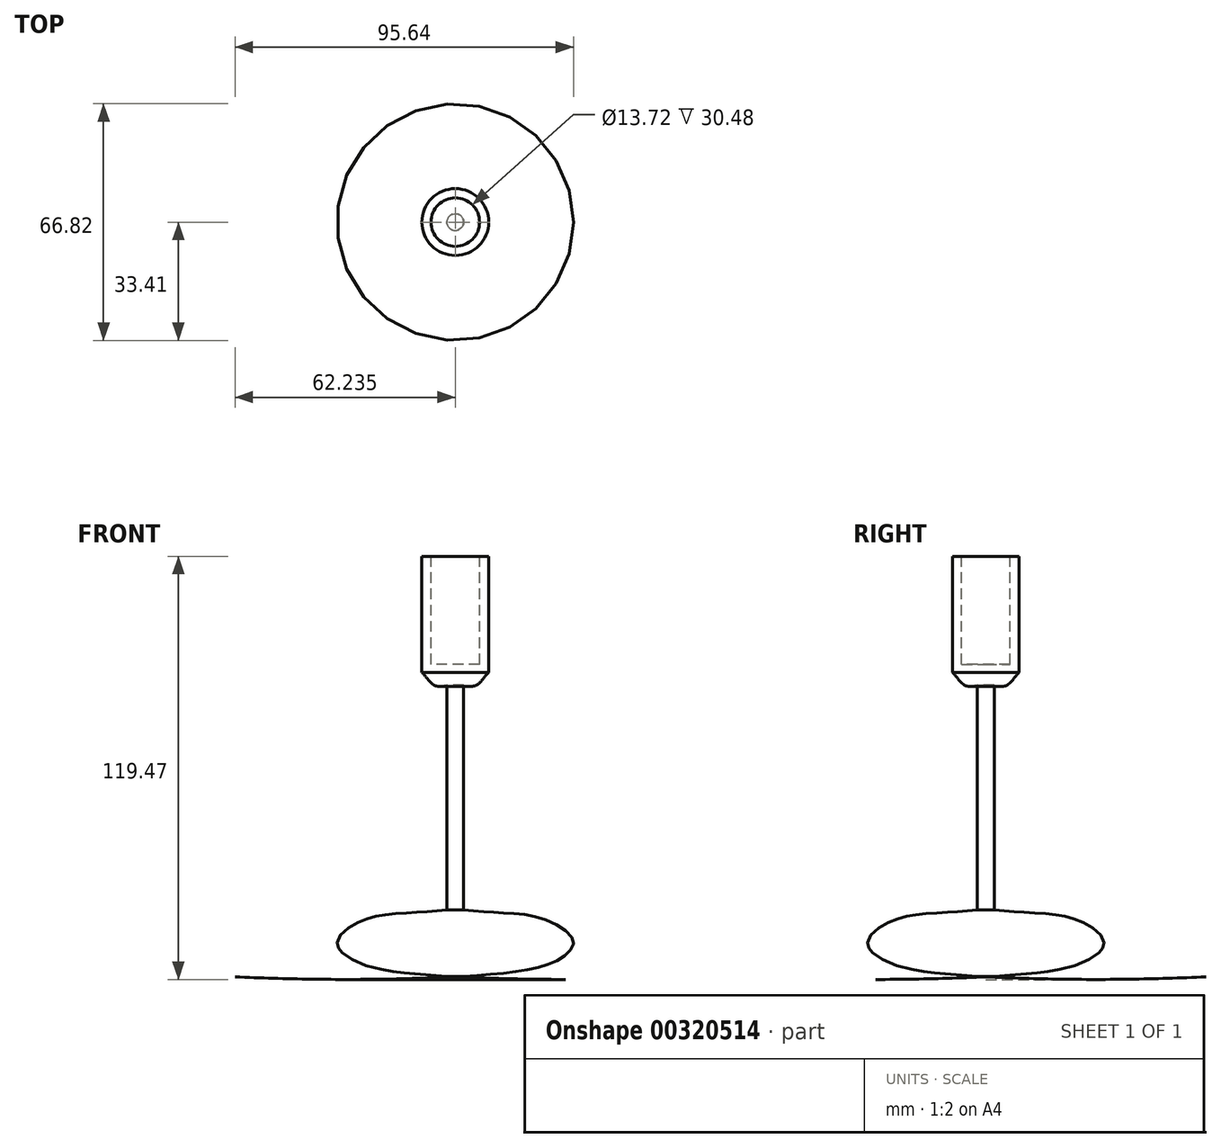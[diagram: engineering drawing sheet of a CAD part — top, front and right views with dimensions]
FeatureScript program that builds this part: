
annotation { "Feature Type Name" : "Feature", "Feature Type Description" : "" }
export const myFeature = defineFeature(function(context is Context, id is Id, definition is map)
    precondition{}
    {
        {
            var Q0;
            Q0=qCreatedBy(makeId("Front.planeOp"),FACE);
            var sketch = newSketch(context, id + "F0", { "sketchPlane" : qUnion([Q0])});
            skFitSpline(sketch, "E0", {"points": [v(7.08, -74.44) * mm, v(-10.6, -72.64) * mm, v(-20.84, -69.06) * mm, v(-23.91, -64.45) * mm, v(-15.72, -58.3) * mm, v(-3.68, -56.5) * mm, v(7.08, -55.74) * mm], "startDerivative": vector(-87.87, 5.95) * mm, "endDerivative": vector(64.33, 5.15) * mm});
            skPoint(sketch, "E1.1.internal.orphan", {"position": v(21.42, -74.44) * mm});
            skFitSpline(sketch, "E2", {"points": [v(11.95, -55.48) * mm, v(22.7, -56) * mm, v(35, -58.56) * mm, v(42.17, -62.65) * mm, v(41.14, -68.8) * mm, v(32.18, -72.13) * mm, v(21.42, -74.44) * mm, v(7.08, -74.44) * mm], "startDerivative": vector(71.75, -0.74) * mm, "endDerivative": vector(-88.62, 4.6) * mm});
            skLineSegment(sketch, "E3", {"start": v(7.08, -55.74) * mm, "end": v(7.08, 7.76) * mm});
            skFitSpline(sketch, "E4", {"points": [v(7.08, 7.76) * mm, v(3.5, 7.76) * mm, v(0, 11.39) * mm], "startDerivative": vector(-7.64, -1.07) * mm, "endDerivative": vector(-6.54, 5.6) * mm});
            skLineSegment(sketch, "E5", {"start": v(0, 11.39) * mm, "end": v(0, 44.15) * mm});
            skFitSpline(sketch, "E6", {"points": [v(11.95, 8.02) * mm, v(16.04, 8.02) * mm, v(19.63, 11.39) * mm], "startDerivative": vector(8.48, -1.02) * mm, "endDerivative": vector(6.9, 5.11) * mm});
            skPoint(sketch, "E7.4.internal.orphan", {"position": v(19.63, 44.15) * mm});
            skFitSpline(sketch, "E8", {"points": [v(0, 44.15) * mm, v(8.1, 44.15) * mm, v(19.63, 44.15) * mm], "startDerivative": vector(16.99, 0) * mm, "endDerivative": vector(22.12, 0) * mm});
            skLineSegment(sketch, "E9", {"start": v(2.58, 44.15) * mm, "end": v(2.58, 13.67) * mm});
            skLineSegment(sketch, "E10", {"start": v(9.44, 13.67) * mm, "end": v(2.58, 13.67) * mm});
            skLineSegment(sketch, "E11", {"start": v(9.44, 53.37) * mm, "end": v(9.44, -81) * mm, "construction": true});
            skLineSegment(sketch, "E12", {"start": v(9.44, -74.56) * mm, "end": v(9.44, 13.67) * mm});
            skSolve(sketch);
        }
        {
            var Q0;
            Q0 = qSketchRegion(id + "F0", true);
            var Q1;
            Q1=sQuery(id+"F0.wireOp",EDGE,"E11");
            revolve(context, id + "F1", {"entities" : qUnion([Q0]), "axis" : qUnion([Q1]), "revolveType" : RevolveType.FULL});
        }
    });
